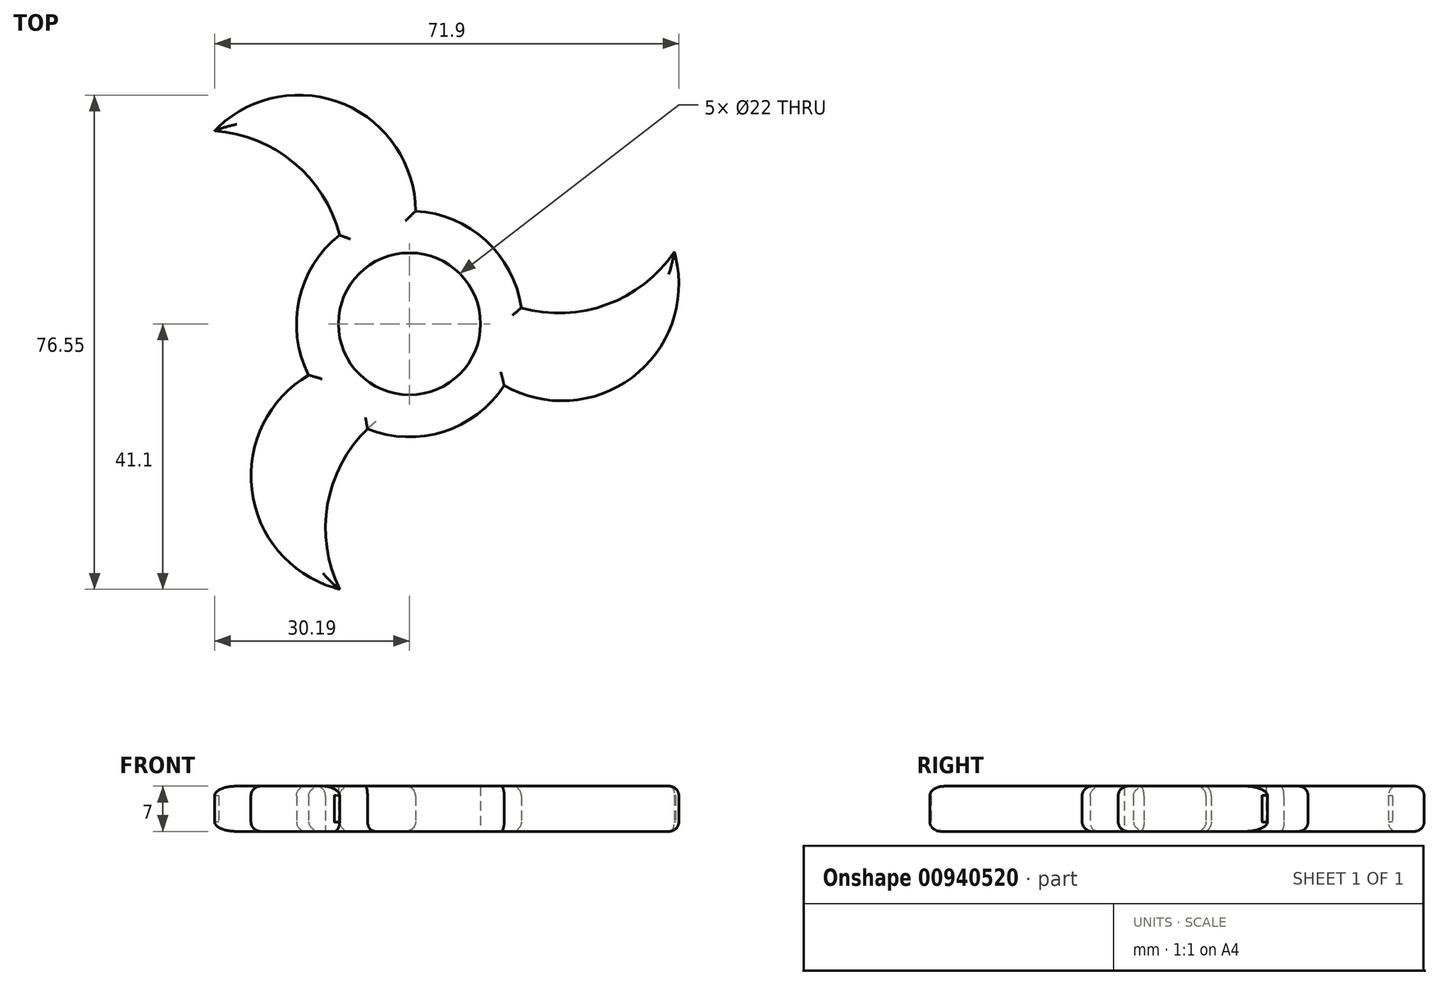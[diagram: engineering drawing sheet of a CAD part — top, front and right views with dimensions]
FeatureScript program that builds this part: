
annotation { "Feature Type Name" : "Feature", "Feature Type Description" : "" }
export const myFeature = defineFeature(function(context is Context, id is Id, definition is map)
    precondition{}
    {
        {
            var Q0;
            Q0=qCreatedBy(makeId("Top.planeOp"),FACE);
            var sketch = newSketch(context, id + "F0", { "sketchPlane" : qUnion([Q0])});
            skCircle(sketch, "E0", {"center": v(0, 0) * mm, "radius": 11 * mm});
            skArc(sketch, "E1", {"start": v(-11.66, -40.87) * mm, "mid": v(-11.24, -40.99) * mm, "end": v(-10.81, -41.1) * mm});
            skArc(sketch, "E2", {"start": v(-6.5, -16.25) * mm, "mid": v(5.28, -16.68) * mm, "end": v(14.66, -9.55) * mm});
            skArc(sketch, "E3", {"start": v(-10.82, 13.75) * mm, "mid": v(-17.89, 24.97) * mm, "end": v(-30.19, 29.91) * mm});
            skArc(sketch, "E4", {"start": v(0.94, 17.47) * mm, "mid": v(-10.44, 34.16) * mm, "end": v(-30.19, 29.91) * mm});
            skArc(sketch, "E5.1.0", {"start": v(-6.5, -16.25) * mm, "mid": v(-12.68, -27.98) * mm, "end": v(-10.81, -41.1) * mm});
            skArc(sketch, "E5.2.0", {"start": v(17.32, 2.5) * mm, "mid": v(30.57, 3) * mm, "end": v(41, 11.19) * mm});
            skArc(sketch, "E6.1.0", {"start": v(-15.6, -7.92) * mm, "mid": v(-24.36, -26.12) * mm, "end": v(-10.81, -41.1) * mm});
            skArc(sketch, "E6.2.0", {"start": v(14.66, -9.55) * mm, "mid": v(34.8, -8.04) * mm, "end": v(41, 11.19) * mm});
            skArc(sketch, "E7.trimOffspring", {"start": v(-29.57, 30.53) * mm, "mid": v(-29.88, 30.22) * mm, "end": v(-30.19, 29.91) * mm});
            skArc(sketch, "E8.trimOffspring", {"start": v(41.22, 10.34) * mm, "mid": v(41.11, 10.76) * mm, "end": v(41, 11.19) * mm});
            skArc(sketch, "E9.trimOffspring", {"start": v(-10.82, 13.75) * mm, "mid": v(-17.09, 3.77) * mm, "end": v(-15.6, -7.92) * mm});
            skArc(sketch, "E10.trimOffspring", {"start": v(17.32, 2.5) * mm, "mid": v(11.8, 12.91) * mm, "end": v(0.94, 17.47) * mm});
            skSolve(sketch);
        }
        {
            var Q0;
            Q0=makeQuery(id+"F0.imprint","IMPRINT",FACE,{"disambiguationData":[TD([[makeQuery(id+"F0.imprint","IMPRINT",EDGE,{"derivedFrom":sQuery(id+"F0.wireOp",EDGE,"E0")}),-1.0]])]});
            extrude(context, id + "F1", {"entities" : qUnion([Q0]), "depth" : 7 * mm, "offsetDistance" : 25 * mm});
        }
        {
            var Q0;
            Q0=makeQuery(id+"F1.opExtrude","CAP_EDGE",EDGE,{"disambiguationData":[OSD([sQuery(id+"F0.wireOp",EDGE,"E6.1.0")])],"isStart":false});
            var Q1;
            Q1=makeQuery(id+"F1.opExtrude","CAP_EDGE",EDGE,{"disambiguationData":[OSD([sQuery(id+"F0.wireOp",EDGE,"E5.2.0")])],"isStart":false});
            var Q2;
            Q2=makeQuery(id+"F1.opExtrude","CAP_EDGE",EDGE,{"disambiguationData":[OSD([sQuery(id+"F0.wireOp",EDGE,"E9.trimOffspring")])],"isStart":false});
            var Q3;
            Q3=makeQuery(id+"F1.opExtrude","CAP_EDGE",EDGE,{"disambiguationData":[OSD([sQuery(id+"F0.wireOp",EDGE,"E10.trimOffspring")])],"isStart":false});
            var Q4;
            Q4=makeQuery(id+"F1.opExtrude","CAP_EDGE",EDGE,{"disambiguationData":[OSD([sQuery(id+"F0.wireOp",EDGE,"E5.1.0")])],"isStart":false});
            var Q5;
            Q5=makeQuery(id+"F1.opExtrude","CAP_EDGE",EDGE,{"disambiguationData":[OSD([sQuery(id+"F0.wireOp",EDGE,"E2")])],"isStart":false});
            var Q6;
            Q6=makeQuery(id+"F1.opExtrude","CAP_EDGE",EDGE,{"disambiguationData":[OSD([sQuery(id+"F0.wireOp",EDGE,"E6.2.0")])],"isStart":false});
            var Q7;
            Q7=makeQuery(id+"F1.opExtrude","CAP_EDGE",EDGE,{"disambiguationData":[OSD([sQuery(id+"F0.wireOp",EDGE,"E4")])],"isStart":false});
            var Q8;
            Q8=makeQuery(id+"F1.opExtrude","CAP_EDGE",EDGE,{"disambiguationData":[OSD([sQuery(id+"F0.wireOp",EDGE,"E3")])],"isStart":false});
            fillet(context, id + "F2", {"entities" : qUnion([Q0, Q1, Q2, Q3, Q4, Q5, Q6, Q7, Q8]), "radius" : 1.5 * mm, "tangentPropagation" : true, "allowEdgeOverflow" : false});
        }
        {
            var Q0;
            Q0=makeQuery(id+"F1.opExtrude","CAP_EDGE",EDGE,{"disambiguationData":[OSD([sQuery(id+"F0.wireOp",EDGE,"E3")])],"isStart":true});
            var Q1;
            Q1=makeQuery(id+"F1.opExtrude","CAP_EDGE",EDGE,{"disambiguationData":[OSD([sQuery(id+"F0.wireOp",EDGE,"E4")])],"isStart":true});
            var Q2;
            Q2=makeQuery(id+"F1.opExtrude","CAP_EDGE",EDGE,{"disambiguationData":[OSD([sQuery(id+"F0.wireOp",EDGE,"E9.trimOffspring")])],"isStart":true});
            var Q3;
            Q3=makeQuery(id+"F1.opExtrude","CAP_EDGE",EDGE,{"disambiguationData":[OSD([sQuery(id+"F0.wireOp",EDGE,"E6.1.0")])],"isStart":true});
            var Q4;
            {var subQ0=sQuery(id+"F0.wireOp",EDGE,"E5.1.0");Q4=makeQuery(id+"F2.opFillet","BLEND_EDGE",EDGE,{"blendedFrom":[makeQuery(id+"F1.opExtrude","CAP_EDGE",EDGE,{"disambiguationData":[OSD([subQ0])],"isStart":true}),makeQuery(id+"F1.opExtrude","CAP_FACE",FACE,{"disambiguationData":[OSD([sQuery(id+"F0.wireOp",EDGE,"E0"),sQuery(id+"F0.wireOp",EDGE,"E1"),sQuery(id+"F0.wireOp",EDGE,"E2"),sQuery(id+"F0.wireOp",EDGE,"E3"),sQuery(id+"F0.wireOp",EDGE,"E4"),subQ0,sQuery(id+"F0.wireOp",EDGE,"E5.2.0"),sQuery(id+"F0.wireOp",EDGE,"E6.1.0"),sQuery(id+"F0.wireOp",EDGE,"E6.2.0"),sQuery(id+"F0.wireOp",EDGE,"E7.trimOffspring"),sQuery(id+"F0.wireOp",EDGE,"E8.trimOffspring"),sQuery(id+"F0.wireOp",EDGE,"E9.trimOffspring"),sQuery(id+"F0.wireOp",EDGE,"E10.trimOffspring")])],"isStart":true})],"blendedInto":[makeQuery(id+"F1.opExtrude","CAP_FACE",FACE,{"disambiguationData":[OSD([sQuery(id+"F0.wireOp",EDGE,"E0"),sQuery(id+"F0.wireOp",EDGE,"E1"),sQuery(id+"F0.wireOp",EDGE,"E2"),sQuery(id+"F0.wireOp",EDGE,"E3"),sQuery(id+"F0.wireOp",EDGE,"E4"),subQ0,sQuery(id+"F0.wireOp",EDGE,"E5.2.0"),sQuery(id+"F0.wireOp",EDGE,"E6.1.0"),sQuery(id+"F0.wireOp",EDGE,"E6.2.0"),sQuery(id+"F0.wireOp",EDGE,"E7.trimOffspring"),sQuery(id+"F0.wireOp",EDGE,"E8.trimOffspring"),sQuery(id+"F0.wireOp",EDGE,"E9.trimOffspring"),sQuery(id+"F0.wireOp",EDGE,"E10.trimOffspring")])],"isStart":true})]});}
            var Q5;
            Q5=makeQuery(id+"F1.opExtrude","CAP_EDGE",EDGE,{"disambiguationData":[OSD([sQuery(id+"F0.wireOp",EDGE,"E2")])],"isStart":true});
            var Q6;
            Q6=makeQuery(id+"F1.opExtrude","CAP_EDGE",EDGE,{"disambiguationData":[OSD([sQuery(id+"F0.wireOp",EDGE,"E6.2.0")])],"isStart":true});
            var Q7;
            Q7=makeQuery(id+"F1.opExtrude","CAP_EDGE",EDGE,{"disambiguationData":[OSD([sQuery(id+"F0.wireOp",EDGE,"E5.2.0")])],"isStart":true});
            var Q8;
            Q8=makeQuery(id+"F1.opExtrude","CAP_EDGE",EDGE,{"disambiguationData":[OSD([sQuery(id+"F0.wireOp",EDGE,"E10.trimOffspring")])],"isStart":true});
            fillet(context, id + "F3", {"entities" : qUnion([Q0, Q1, Q2, Q3, Q4, Q5, Q6, Q7, Q8]), "radius" : 1.5 * mm, "tangentPropagation" : true, "allowEdgeOverflow" : false});
        }
    });
